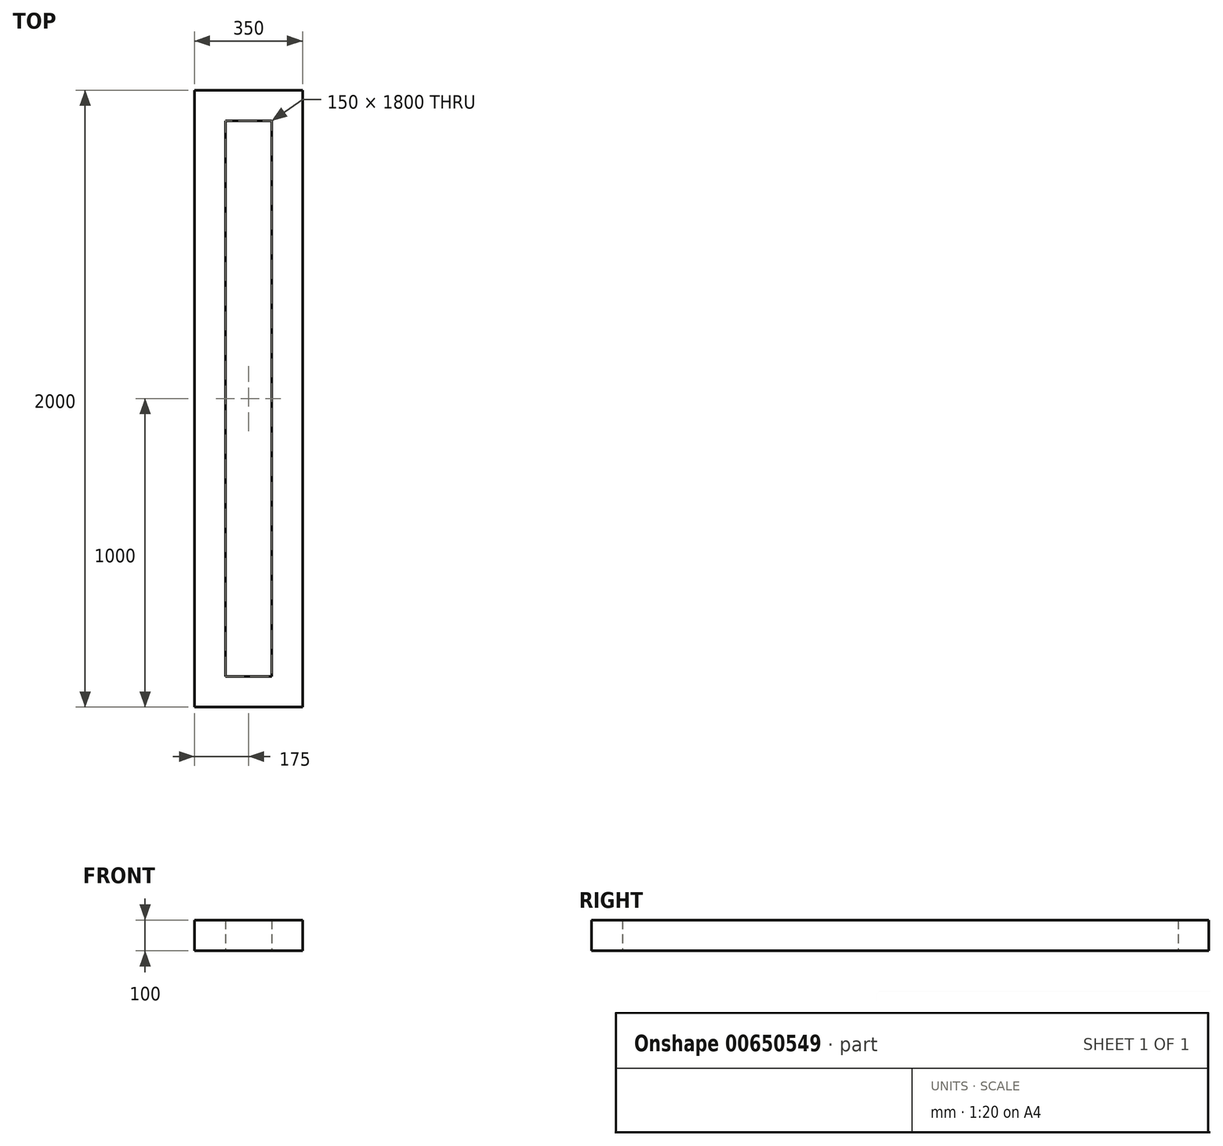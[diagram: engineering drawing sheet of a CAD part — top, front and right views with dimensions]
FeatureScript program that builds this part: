
annotation { "Feature Type Name" : "Feature", "Feature Type Description" : "" }
export const myFeature = defineFeature(function(context is Context, id is Id, definition is map)
    precondition{}
    {
        {
            var Q0;
            Q0=qCreatedBy(makeId("Top.planeOp"),FACE);
            var sketch = newSketch(context, id + "F0", { "sketchPlane" : qUnion([Q0])});
            skLineSegment(sketch, "E0.bottom", {"start": v(0, 0) * mm, "end": v(-350, 0) * mm});
            skLineSegment(sketch, "E0.top", {"start": v(0, 2000) * mm, "end": v(-350, 2000) * mm});
            skLineSegment(sketch, "E0.left", {"start": v(0, 0) * mm, "end": v(0, 2000) * mm});
            skLineSegment(sketch, "E0.right", {"start": v(-350, 0) * mm, "end": v(-350, 2000) * mm});
            skLineSegment(sketch, "E1.bottom", {"start": v(-100, 100) * mm, "end": v(-250, 100) * mm});
            skLineSegment(sketch, "E1.top", {"start": v(-100, 1900) * mm, "end": v(-250, 1900) * mm});
            skLineSegment(sketch, "E1.left", {"start": v(-100, 100) * mm, "end": v(-100, 1900) * mm});
            skLineSegment(sketch, "E1.right", {"start": v(-250, 100) * mm, "end": v(-250, 1900) * mm});
            skSolve(sketch);
        }
        {
            var Q0;
            Q0 = qSketchRegion(id + "F0", true);
            extrude(context, id + "F1", {"entities" : qUnion([Q0]), "depth" : 100 * mm, "offsetDistance" : 25 * mm});
        }
    });
